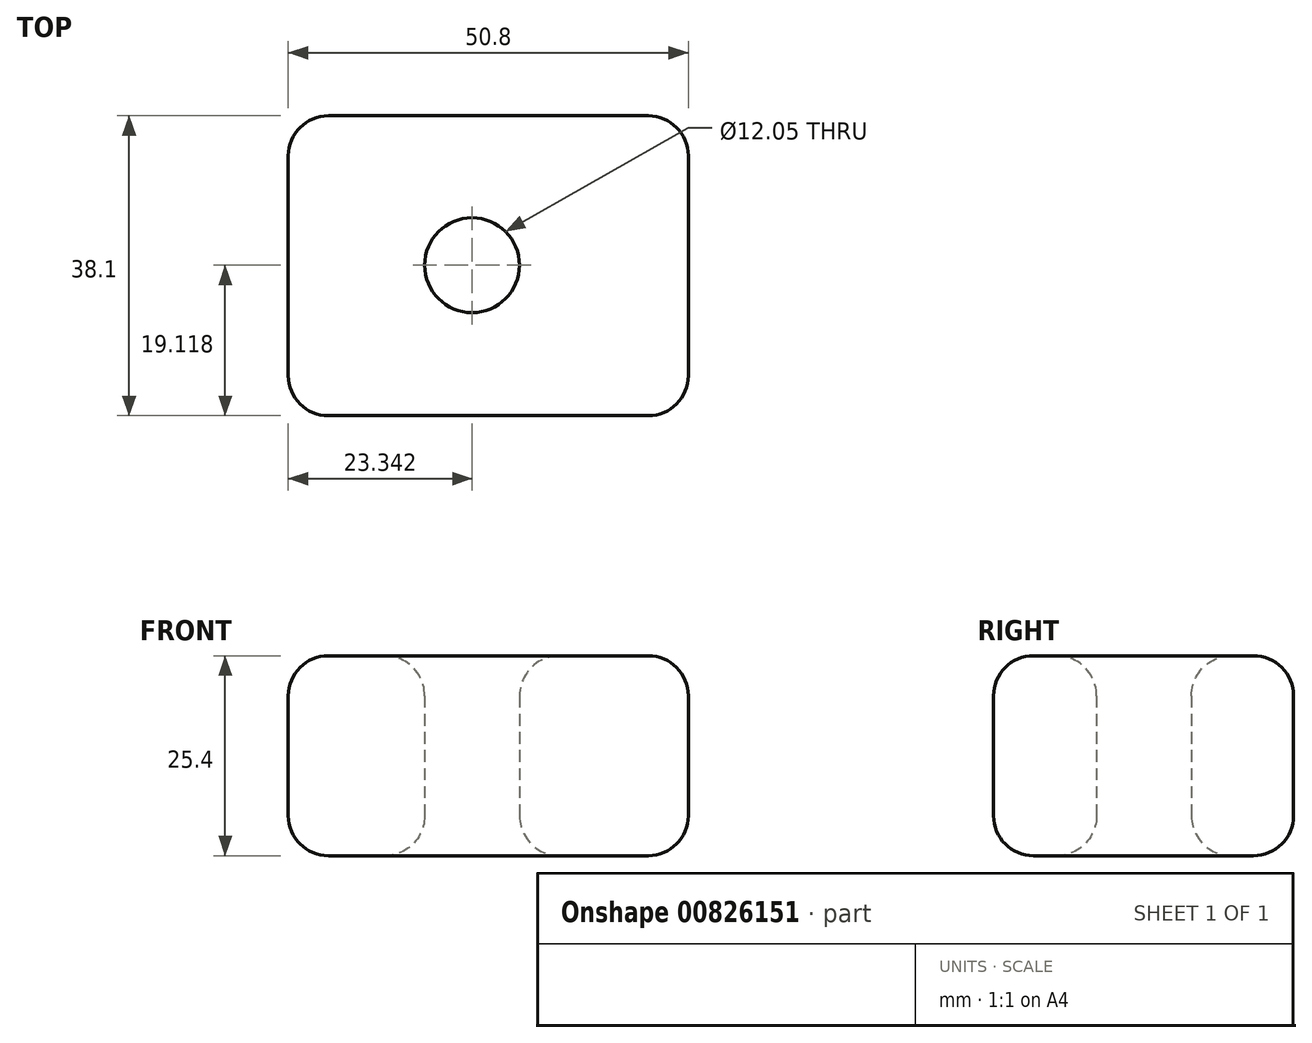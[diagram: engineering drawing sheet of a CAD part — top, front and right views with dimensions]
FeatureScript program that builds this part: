
annotation { "Feature Type Name" : "Feature", "Feature Type Description" : "" }
export const myFeature = defineFeature(function(context is Context, id is Id, definition is map)
    precondition{}
    {
        {
            var Q0;
            Q0=qCreatedBy(makeId("Top.planeOp"),FACE);
            var sketch = newSketch(context, id + "F0", { "sketchPlane" : qUnion([Q0])});
            skLineSegment(sketch, "E0.bottom", {"start": v(0, 0) * mm, "end": v(50.8, 0) * mm});
            skLineSegment(sketch, "E0.top", {"start": v(0, 38.1) * mm, "end": v(50.8, 38.1) * mm});
            skLineSegment(sketch, "E0.left", {"start": v(0, 0) * mm, "end": v(0, 38.1) * mm});
            skLineSegment(sketch, "E0.right", {"start": v(50.8, 0) * mm, "end": v(50.8, 38.1) * mm});
            skCircle(sketch, "E1", {"center": v(23.34, 19.12) * mm, "radius": 6.02 * mm});
            skSolve(sketch);
        }
        {
            var Q0;
            Q0 = qSketchRegion(id + "F0", true);
            extrude(context, id + "F1", {"entities" : qUnion([Q0]), "depth" : 25.4 * mm, "offsetDistance" : 25.4 * mm});
        }
        {
            var Q0;
            Q0=makeQuery(id+"F1.opExtrude","SWEPT_FACE",FACE,{"disambiguationData":[OSD([sQuery(id+"F0.wireOp",EDGE,"E0.right")])]});
            var Q1;
            Q1=makeQuery(id+"F1.opExtrude","SWEPT_FACE",FACE,{"disambiguationData":[OSD([sQuery(id+"F0.wireOp",EDGE,"E0.left")])]});
            var Q2;
            Q2=makeQuery(id+"F1.opExtrude","CAP_FACE",FACE,{"disambiguationData":[OSD([sQuery(id+"F0.wireOp",EDGE,"E0.bottom"),sQuery(id+"F0.wireOp",EDGE,"E0.top"),sQuery(id+"F0.wireOp",EDGE,"E0.left"),sQuery(id+"F0.wireOp",EDGE,"E0.right")])],"isStart":false});
            var Q3;
            Q3=makeQuery(id+"F1.opExtrude","CAP_FACE",FACE,{"disambiguationData":[OSD([sQuery(id+"F0.wireOp",EDGE,"E0.bottom"),sQuery(id+"F0.wireOp",EDGE,"E0.top"),sQuery(id+"F0.wireOp",EDGE,"E0.left"),sQuery(id+"F0.wireOp",EDGE,"E0.right")])],"isStart":true});
            fillet(context, id + "F2", {"entities" : qUnion([Q0, Q1, Q2, Q3]), "radius" : 5.08 * mm, "tangentPropagation" : true, "allowEdgeOverflow" : false});
        }
    });
